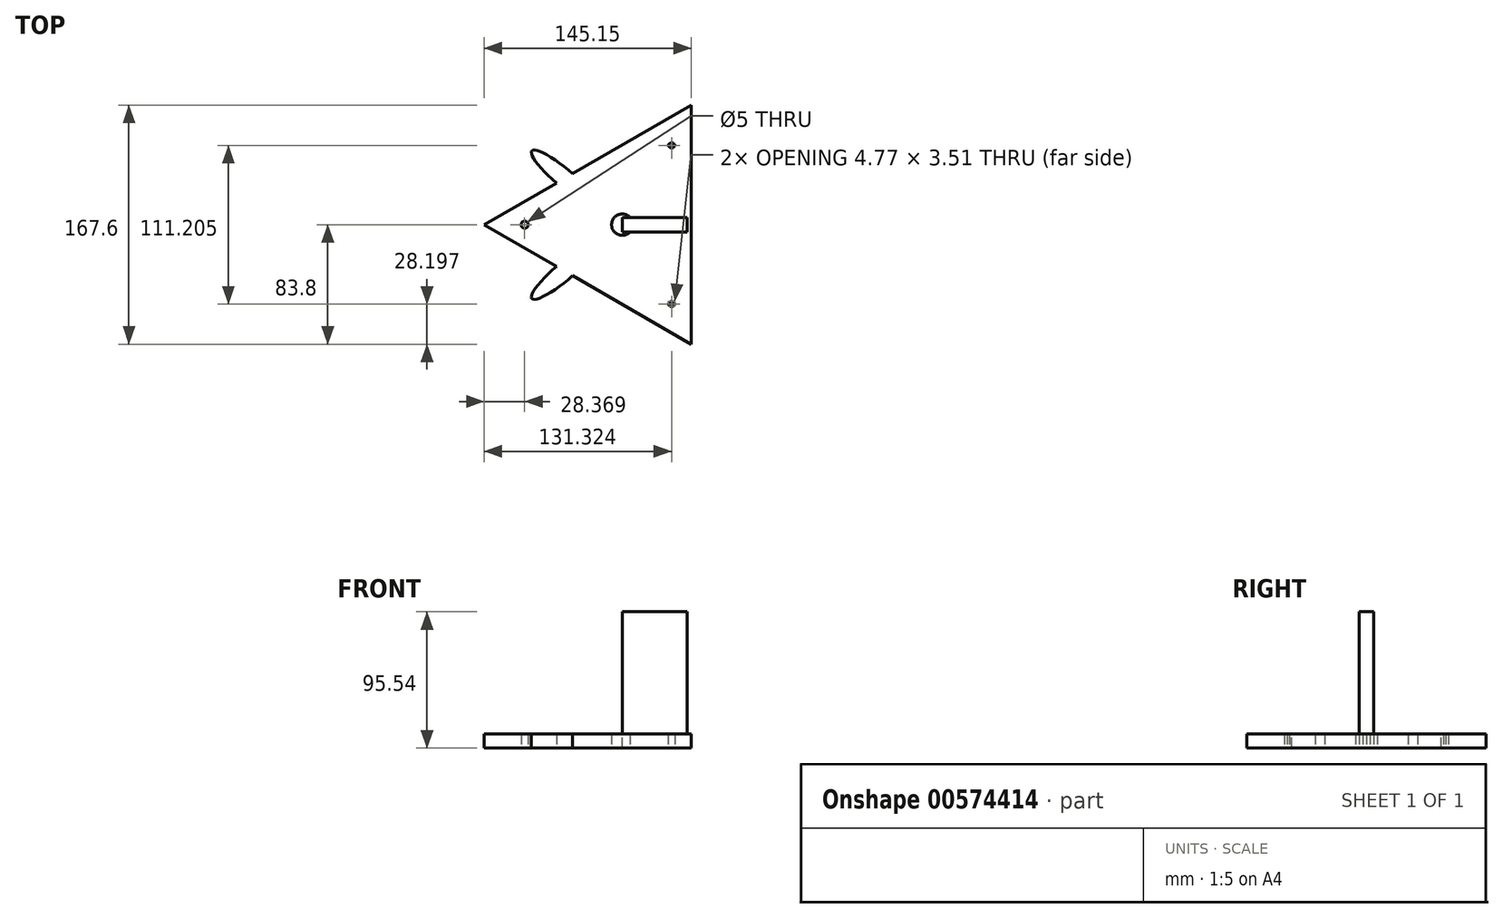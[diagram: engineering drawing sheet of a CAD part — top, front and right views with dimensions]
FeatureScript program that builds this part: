
annotation { "Feature Type Name" : "Feature", "Feature Type Description" : "" }
export const myFeature = defineFeature(function(context is Context, id is Id, definition is map)
    precondition{}
    {
        {
            var Q0;
            Q0=qCreatedBy(makeId("Top.planeOp"),FACE);
            var sketch = newSketch(context, id + "F0", { "sketchPlane" : qUnion([Q0])});
            skCircle(sketch, "E0.cCircle", {"center": v(0, 0) * mm, "radius": 48.38 * mm, "construction": true});
            skLineSegment(sketch, "E0.0", {"start": v(48.38, 83.8) * mm, "end": v(48.38, -83.8) * mm});
            skLineSegment(sketch, "E0.1", {"start": v(48.38, -83.8) * mm, "end": v(-96.77, 0) * mm});
            skLineSegment(sketch, "E0.2", {"start": v(-96.77, 0) * mm, "end": v(48.38, 83.8) * mm});
            skPoint(sketch, "E0.0.midPoint", {"position": v(48.38, 0) * mm});
            skSolve(sketch);
        }
        {
            var Q0;
            Q0=qCreatedBy(makeId("Top.planeOp"),FACE);
            var sketch = newSketch(context, id + "F1", { "sketchPlane" : qUnion([Q0])});
            skLineSegment(sketch, "E1", {"start": v(-68.4, 0) * mm, "end": v(34.55, 56.35) * mm});
            skLineSegment(sketch, "E2", {"start": v(34.55, 56.35) * mm, "end": v(34.55, -54.86) * mm});
            skLineSegment(sketch, "E3", {"start": v(34.55, -54.86) * mm, "end": v(-68.4, 0) * mm});
            skSolve(sketch);
        }
        {
            var Q0;
            Q0=makeQuery(id+"F0.imprint","IMPRINT",FACE,{"disambiguationData":[TD([[makeQuery(id+"F0.imprint","IMPRINT",EDGE,{"derivedFrom":sQuery(id+"F0.wireOp",EDGE,"E0.0")}),-1.0]])]});
            extrude(context, id + "F2", {"entities" : qUnion([Q0]), "depth" : 10 * mm, "offsetDistance" : 25 * mm});
        }
        {
            var Q0;
            Q0=sQuery(id+"F1.wireOp",VERTEX,"E2.start");
            var Q1;
            Q1=sQuery(id+"F1.wireOp",VERTEX,"E2.end");
            var Q2;
            Q2=sQuery(id+"F1.wireOp",VERTEX,"E1.start");
            var Q3;
            Q3=makeQuery(id+"F2.opExtrude","SWEPT_BODY",BODY,{"disambiguationData":[OSD([sQuery(id+"F0.wireOp",EDGE,"E0.0"),sQuery(id+"F0.wireOp",EDGE,"E0.1"),sQuery(id+"F0.wireOp",EDGE,"E0.2")])]});
            hole(context, id + "F3", {"style" : HoleStyle.SIMPLE, "endStyle" : HoleEndStyle.THROUGH, "oppositeDirection" : true, "holeDiameter" : 5 * mm, "isTappedThrough" : true, "tappedDepth" : 12 * mm, "tapClearance" : 3, "locations" : qUnion([Q0, Q1, Q2]), "scope" : qUnion([Q3])});
        }
        {
            var Q0;
            Q0=qCreatedBy(makeId("Top.planeOp"),FACE);
            var sketch = newSketch(context, id + "F4", { "sketchPlane" : qUnion([Q0])});
            skPoint(sketch, "E4", {"position": v(0, 0) * mm});
            skSolve(sketch);
        }
        {
            var Q0;
            Q0=sQuery(id+"F4.wireOp",VERTEX,"E4");
            var Q1;
            Q1=makeQuery(id+"F2.opExtrude","SWEPT_BODY",BODY,{"disambiguationData":[OSD([sQuery(id+"F0.wireOp",EDGE,"E0.0"),sQuery(id+"F0.wireOp",EDGE,"E0.1"),sQuery(id+"F0.wireOp",EDGE,"E0.2")])]});
            hole(context, id + "F5", {"style" : HoleStyle.SIMPLE, "endStyle" : HoleEndStyle.THROUGH, "oppositeDirection" : true, "holeDiameter" : 15 * mm, "isTappedThrough" : true, "tappedDepth" : 12 * mm, "tapClearance" : 3, "locations" : qUnion([Q0]), "scope" : qUnion([Q1])});
        }
        {
            var Q0;
            Q0=qCreatedBy(makeId("Top.planeOp"),FACE);
            var sketch = newSketch(context, id + "F6", { "sketchPlane" : qUnion([Q0])});
            skEllipse(sketch, "E5", {"center": v(-41.8, -33.71) * mm, "majorRadius": 28.08 * mm, "minorRadius": 6.12 * mm, "majorAxis": v(-0.77, -0.64)});
            skSolve(sketch);
        }
        {
            var Q0;
            Q0=makeQuery(id+"F6.imprint","IMPRINT",FACE,{"disambiguationData":[TD([[makeQuery(id+"F6.imprint","IMPRINT",EDGE,{"derivedFrom":sQuery(id+"F6.wireOp",EDGE,"E5")}),1.0]])]});
            extrude(context, id + "F7", {"entities" : qUnion([Q0]), "operationType" : NewBodyOperationType.ADD, "depth" : 10 * mm, "offsetDistance" : 25 * mm});
        }
        {
            var Q0;
            Q0=makeQuery(id+"F2.opExtrude","SWEPT_BODY",BODY,{"disambiguationData":[OSD([sQuery(id+"F0.wireOp",EDGE,"E0.0"),sQuery(id+"F0.wireOp",EDGE,"E0.1"),sQuery(id+"F0.wireOp",EDGE,"E0.2")])]});
            var Q1;
            Q1=qCreatedBy(makeId("Front.planeOp"),FACE);
            mirror(context, id + "F8", {"operationType" : NewBodyOperationType.ADD, "entities" : qUnion([Q0]), "mirrorPlane" : qUnion([Q1])});
        }
        {
            var Q0;
            Q0=qCreatedBy(makeId("Front.planeOp"),FACE);
            var sketch = newSketch(context, id + "F9", { "sketchPlane" : qUnion([Q0])});
            skLineSegment(sketch, "E6.bottom", {"start": v(0, 0) * mm, "end": v(45.59, 0) * mm});
            skLineSegment(sketch, "E6.top", {"start": v(0, 95.54) * mm, "end": v(45.59, 95.54) * mm});
            skLineSegment(sketch, "E6.left", {"start": v(0, 0) * mm, "end": v(0, 95.54) * mm});
            skLineSegment(sketch, "E6.right", {"start": v(45.59, 0) * mm, "end": v(45.59, 95.54) * mm});
            skSolve(sketch);
        }
        {
            var Q0;
            Q0=makeQuery(id+"F9.imprint","IMPRINT",FACE,{"disambiguationData":[TD([[makeQuery(id+"F9.imprint","IMPRINT",EDGE,{"derivedFrom":sQuery(id+"F9.wireOp",EDGE,"E6.bottom")}),1.0]])]});
            extrude(context, id + "F10", {"entities" : qUnion([Q0]), "operationType" : NewBodyOperationType.ADD, "depth" : 5 * mm, "offsetDistance" : 25 * mm});
        }
        {
            var Q0;
            Q0=makeQuery(id+"F2.opExtrude","SWEPT_BODY",BODY,{"disambiguationData":[OSD([sQuery(id+"F0.wireOp",EDGE,"E0.0"),sQuery(id+"F0.wireOp",EDGE,"E0.1"),sQuery(id+"F0.wireOp",EDGE,"E0.2")])]});
            var Q1;
            Q1=qCreatedBy(makeId("Front.planeOp"),FACE);
            mirror(context, id + "F11", {"operationType" : NewBodyOperationType.ADD, "entities" : qUnion([Q0]), "mirrorPlane" : qUnion([Q1])});
        }
    });
